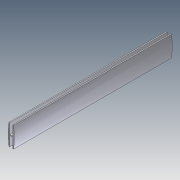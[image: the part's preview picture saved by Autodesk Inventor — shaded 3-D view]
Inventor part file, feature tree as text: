
AUTODESK INVENTOR PART (.ipt)
format: ipt  version: 2012 (Build 160160000, 160)  size: 90,112 bytes
history: native  units: in
note: dims shown in document units (in); Inventor stores cm internally (conversion verified against a paired STEP export)
features: extrude x1, sketch x1
ambient origin geometry x8: Origin, YZ Plane, XZ Plane, XY Plane, X Axis, Y Axis, Z Axis, Center Point
bodies: Solid1 (feature_tree)
feature tree (2):
  extrude  "Extrusion1"  Depth=0.0781in
  sketch  "Sketch1"  dims[d0=0.5234in d1=1.0469in d2=0.0781in d3=0.1562in d4=0.0781in d5=0.1562in d6=0.0234in d7=0.0469in d8=0.5234in d9=1.0469in d10=4.0in d12=0.0469in d13=8.0in d14=0.0in]
